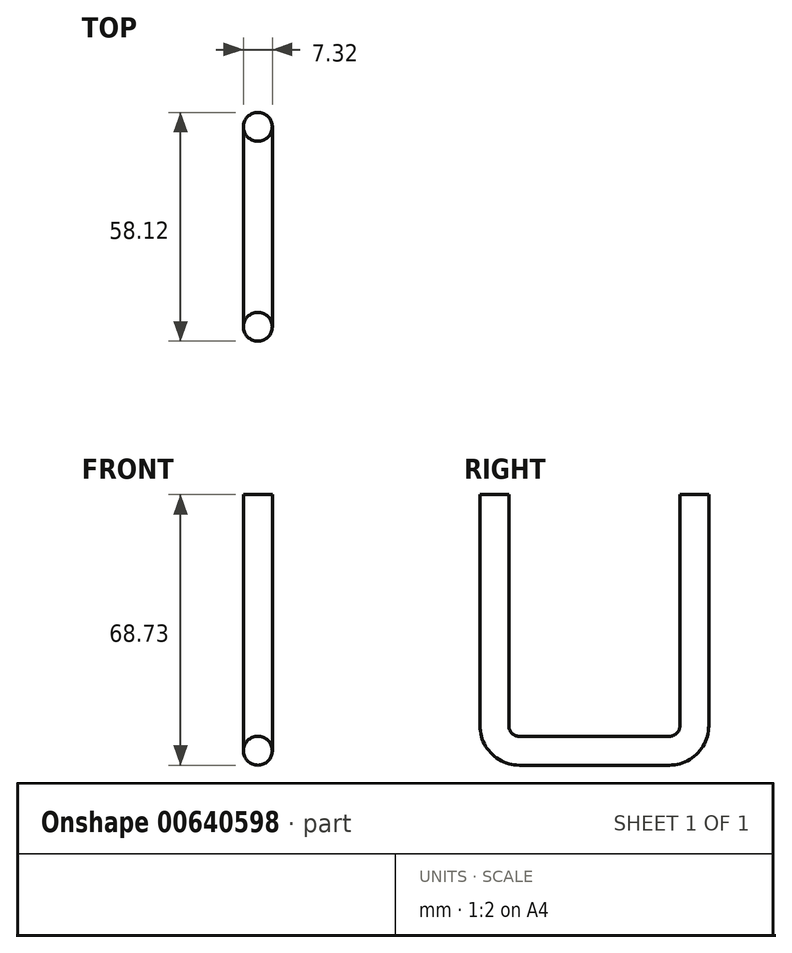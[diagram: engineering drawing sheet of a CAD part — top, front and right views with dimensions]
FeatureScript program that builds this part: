
annotation { "Feature Type Name" : "Feature", "Feature Type Description" : "" }
export const myFeature = defineFeature(function(context is Context, id is Id, definition is map)
    precondition{}
    {
        {
            var Q0;
            Q0=qCreatedBy(makeId("Right.planeOp"),FACE);
            var sketch = newSketch(context, id + "F0", { "sketchPlane" : qUnion([Q0])});
            skLineSegment(sketch, "E0", {"start": v(0, 0) * mm, "end": v(0, -33.31) * mm});
            skLineSegment(sketch, "E1", {"start": v(-6.35, -39.66) * mm, "end": v(-44.45, -39.66) * mm});
            skLineSegment(sketch, "E2", {"start": v(-50.8, -33.31) * mm, "end": v(-50.8, 0) * mm});
            skPoint(sketch, "E3.visualSharp", {"position": v(0, -39.66) * mm});
            skArc(sketch, "E3.filletArc", {"start": v(-6.35, -39.66) * mm, "mid": v(-1.86, -37.8) * mm, "end": v(0, -33.31) * mm});
            skPoint(sketch, "E4.visualSharp", {"position": v(-50.8, -39.66) * mm});
            skArc(sketch, "E4.filletArc", {"start": v(-50.8, -33.31) * mm, "mid": v(-48.94, -37.8) * mm, "end": v(-44.45, -39.66) * mm});
            skSolve(sketch);
        }
        {
            var Q0;
            Q0=qCreatedBy(makeId("Top.planeOp"),FACE);
            var sketch = newSketch(context, id + "F1", { "sketchPlane" : qUnion([Q0])});
            skCircle(sketch, "E5", {"center": v(0, 0) * mm, "radius": 3.66 * mm});
            skSolve(sketch);
        }
        {
            var Q0;
            Q0=makeQuery(id+"F1.imprint","IMPRINT",FACE,{"disambiguationData":[TD([[makeQuery(id+"F1.imprint","IMPRINT",EDGE,{"derivedFrom":sQuery(id+"F1.wireOp",EDGE,"E5")}),1.0]])]});
            var Q1;
            Q1=sQuery(id+"F0.wireOp",EDGE,"E0");
            var Q2;
            Q2=sQuery(id+"F0.wireOp",EDGE,"E3.filletArc");
            var Q3;
            Q3=sQuery(id+"F0.wireOp",EDGE,"E1");
            var Q4;
            Q4=sQuery(id+"F0.wireOp",EDGE,"E4.filletArc");
            var Q5;
            Q5=sQuery(id+"F0.wireOp",EDGE,"E2");
            sweep(context, id + "F2", {"profiles" : qUnion([Q0]), "path" : qUnion([Q1, Q2, Q3, Q4, Q5])});
        }
        {
            var Q0;
            Q0=makeQuery(id+"F2.opSweep","CAP_FACE",FACE,{"disambiguationData":[OSD([sQuery(id+"F0.wireOp",VERTEX,"E2.end"),sQuery(id+"F1.wireOp",EDGE,"E5")])],"isStart":false});
            var Q1;
            Q1=makeQuery(id+"F2.opSweep","CAP_FACE",FACE,{"disambiguationData":[OSD([sQuery(id+"F0.wireOp",VERTEX,"E0.start"),sQuery(id+"F1.wireOp",EDGE,"E5")])],"isStart":true});
            extrude(context, id + "F3", {"entities" : qUnion([Q0, Q1]), "operationType" : NewBodyOperationType.ADD, "depth" : 25.4 * mm, "offsetDistance" : 25.4 * mm});
        }
    });
